# Revit family: CENTUM Ecklasche L
name_source: partatom
category: HLS-Bauteile
revit_build: Autodesk Revit 2017 (Build: 20190507_1515(x64)
units: mm (PartAtom-declared; Revit-internal decimal feet)

## family parameters
Arbeitsebenenbasiert = Ja
Beim Laden mit Abzugskörper schneiden = Nein
Bemaßung runder Anschluss = Durchmesser verwenden
Gemeinsam genutzt = Ja
Immer vertikal = Nein
Raumberechnungspunkt = Nein
Teiletyp = Normal

## types (1)
- CENTUM Ecklasche L
    Artikelnummer = 1640003010
    EAN = 4250928436887
    Fabrikat = MEFA
    Firma = MEFA Befestigungs- und Montagesysteme GmbH
    Gewicht = 1.38 kg
    Gewicht pro Bauteil = 1.38 kg
    Kurztext1 = Ecklasche
    Kurztext2 = für Centum XL 100, 120, 200
    Langloch = 14x40 mm
    Länge Schenkel 1 = 0 mm  [stored 0 ft]
    Länge Schenkel 2 = 0 mm  [stored 0 ft]
    Material = Stahl
    Mengeneinheit = St
    Oberflaeche = feuerstückverzinkt
    Profil = CENTUM
    Profiltyp = XL 100, XL 120, XL 200
    Sicherheitsfaktor = 1.54
    Stärke Material = 0 mm  [stored 0 ft]
    Vorgabe-Ansicht = 1219 mm
    max. Rohraußendurchmesser = 0 mm  [stored 0 ft]
    min. Rohraußendurchmesser = 0 mm  [stored 0 ft]
    vpe = 1 St

note: [stored X ft] marks values corroborated as IEEE doubles in the binary element streams (Revit-internal decimal feet)
